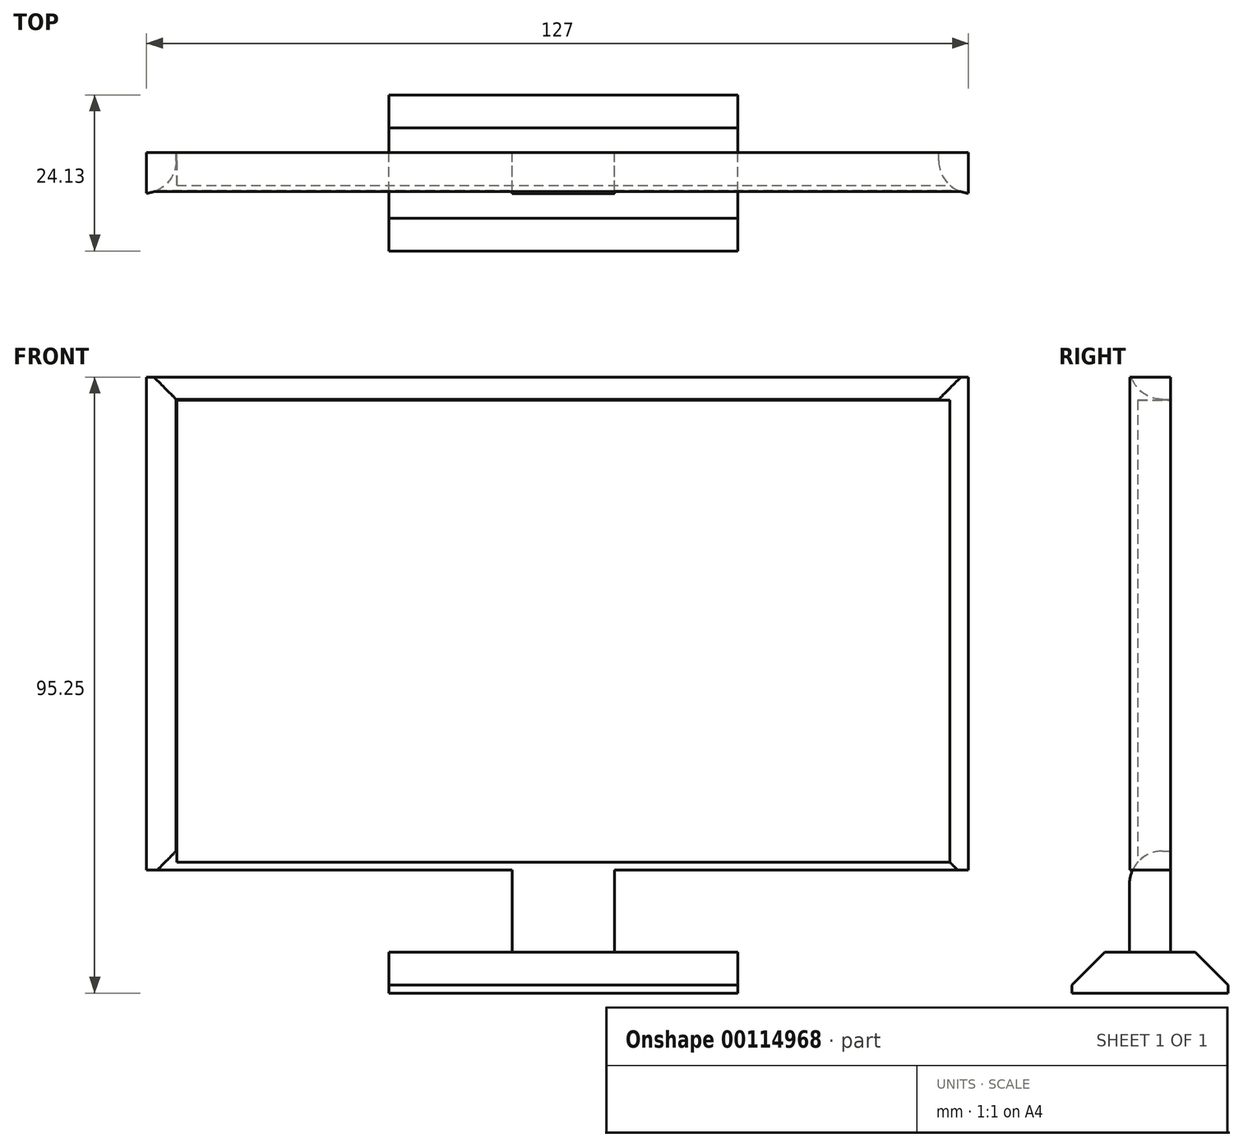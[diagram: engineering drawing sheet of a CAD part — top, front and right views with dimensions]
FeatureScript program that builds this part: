
annotation { "Feature Type Name" : "Feature", "Feature Type Description" : "" }
export const myFeature = defineFeature(function(context is Context, id is Id, definition is map)
    precondition{}
    {
        {
            var Q0;
            Q0=qCreatedBy(makeId("Front.planeOp"),FACE);
            var sketch = newSketch(context, id + "F0", { "sketchPlane" : qUnion([Q0])});
            skLineSegment(sketch, "E0", {"start": v(-63.78, 41.47) * mm, "end": v(63.22, 41.47) * mm});
            skLineSegment(sketch, "E1", {"start": v(-63.78, 41.47) * mm, "end": v(-63.78, -34.73) * mm});
            skLineSegment(sketch, "E2", {"start": v(63.22, 41.47) * mm, "end": v(63.22, -34.73) * mm});
            skLineSegment(sketch, "E3", {"start": v(63.22, -34.73) * mm, "end": v(-63.78, -34.73) * mm});
            skLineSegment(sketch, "E4", {"start": v(8.52, -34.73) * mm, "end": v(8.52, -47.43) * mm});
            skLineSegment(sketch, "E5", {"start": v(-59.2, 38.02) * mm, "end": v(-59.2, -31.83) * mm});
            skLineSegment(sketch, "E6", {"start": v(-59.2, 38.02) * mm, "end": v(58.63, 38.02) * mm});
            skLineSegment(sketch, "E7", {"start": v(58.63, 38.02) * mm, "end": v(58.63, -31.83) * mm});
            skLineSegment(sketch, "E8", {"start": v(-59.2, -31.83) * mm, "end": v(58.63, -31.83) * mm});
            skLineSegment(sketch, "E9", {"start": v(8.52, -47.43) * mm, "end": v(27.57, -47.43) * mm});
            skLineSegment(sketch, "E10", {"start": v(27.57, -47.43) * mm, "end": v(27.57, -53.78) * mm});
            skLineSegment(sketch, "E11", {"start": v(63.22, 15.64) * mm, "end": v(58.63, 15.64) * mm, "construction": true});
            skLineSegment(sketch, "E12", {"start": v(-63.78, 3.1) * mm, "end": v(-59.2, 3.37) * mm, "construction": true});
            skPoint(sketch, "E12.startSnap0", {"position": v(-59.2, 3.1) * mm});
            skPoint(sketch, "E12.endSnap0", {"position": v(-63.78, 3.37) * mm});
            skPoint(sketch, "E12.endSnap1", {"position": v(-59.2, 3.1) * mm});
            skLineSegment(sketch, "E13", {"start": v(-7.28, -34.73) * mm, "end": v(-7.28, -47.43) * mm});
            skLineSegment(sketch, "E14", {"start": v(-7.28, -47.43) * mm, "end": v(-26.33, -47.43) * mm});
            skLineSegment(sketch, "E15", {"start": v(27.57, -53.78) * mm, "end": v(-26.33, -53.78) * mm});
            skLineSegment(sketch, "E16", {"start": v(-26.33, -53.78) * mm, "end": v(-26.33, -47.43) * mm});
            skLineSegment(sketch, "E17", {"start": v(-7.28, -34.73) * mm, "end": v(8.52, -34.73) * mm});
            skLineSegment(sketch, "E18", {"start": v(8.52, -34.73) * mm, "end": v(-7.28, -34.73) * mm});
            skLineSegment(sketch, "E19", {"start": v(8.52, -47.43) * mm, "end": v(-7.28, -47.43) * mm});
            skSolve(sketch);
        }
        {
            var Q0;
            Q0 = qSketchRegion(id + "F0", true);
            extrude(context, id + "F1", {"entities" : qUnion([Q0]), "depth" : 6.35 * mm});
        }
        {
            var Q0;
            Q0=qCreatedBy(makeId("Front.planeOp"),FACE);
            var sketch = newSketch(context, id + "F2", { "sketchPlane" : qUnion([Q0])});
            skLineSegment(sketch, "E20.bottom", {"start": v(-59.13, 37.88) * mm, "end": v(59.35, 37.88) * mm});
            skLineSegment(sketch, "E20.top", {"start": v(-59.13, -31.88) * mm, "end": v(59.35, -31.88) * mm});
            skLineSegment(sketch, "E20.left", {"start": v(-59.13, 37.88) * mm, "end": v(-59.13, -31.88) * mm});
            skLineSegment(sketch, "E20.right", {"start": v(59.35, 37.88) * mm, "end": v(59.35, -31.88) * mm});
            skSolve(sketch);
        }
        {
            var Q0;
            Q0=makeQuery(id+"F2.imprint","IMPRINT",FACE,{"disambiguationData":[TD([[makeQuery(id+"F2.imprint","IMPRINT",EDGE,{"derivedFrom":sQuery(id+"F2.wireOp",EDGE,"E20.bottom")}),-1.0]])]});
            extrude(context, id + "F3", {"entities" : qUnion([Q0]), "operationType" : NewBodyOperationType.ADD, "depth" : 5.08 * mm});
        }
        {
            var Q0;
            Q0=makeQuery(id+"F1.opExtrude","CAP_EDGE",EDGE,{"disambiguationData":[OSD([sQuery(id+"F0.wireOp",EDGE,"E8")])],"isStart":false});
            var Q1;
            Q1=makeQuery(id+"F1.opExtrude","CAP_EDGE",EDGE,{"disambiguationData":[OSD([sQuery(id+"F0.wireOp",EDGE,"E6")])],"isStart":false});
            var Q2;
            Q2=makeQuery(id+"F1.opExtrude","CAP_EDGE",EDGE,{"disambiguationData":[OSD([sQuery(id+"F0.wireOp",EDGE,"E5")])],"isStart":false});
            var Q3;
            Q3=makeQuery(id+"F1.opExtrude","CAP_EDGE",EDGE,{"disambiguationData":[OSD([sQuery(id+"F0.wireOp",EDGE,"E7")])],"isStart":false});
            fillet(context, id + "F4", {"entities" : qUnion([Q0, Q1, Q2, Q3]), "radius" : 5.08 * mm, "tangentPropagation" : true, "allowEdgeOverflow" : false});
        }
        {
            var Q0;
            Q0=makeQuery(id+"F1.opExtrude","CAP_FACE",FACE,{"disambiguationData":[OSD([sQuery(id+"F0.wireOp",EDGE,"E0"),sQuery(id+"F0.wireOp",EDGE,"E1"),sQuery(id+"F0.wireOp",EDGE,"E2"),sQuery(id+"F0.wireOp",EDGE,"E3"),sQuery(id+"F0.wireOp",EDGE,"E4"),sQuery(id+"F0.wireOp",EDGE,"E5"),sQuery(id+"F0.wireOp",EDGE,"E6"),sQuery(id+"F0.wireOp",EDGE,"E7"),sQuery(id+"F0.wireOp",EDGE,"E8"),sQuery(id+"F0.wireOp",EDGE,"E9"),sQuery(id+"F0.wireOp",EDGE,"E10"),sQuery(id+"F0.wireOp",EDGE,"E13"),sQuery(id+"F0.wireOp",EDGE,"E14"),sQuery(id+"F0.wireOp",EDGE,"E15"),sQuery(id+"F0.wireOp",EDGE,"E16")])],"isStart":false});
            var sketch = newSketch(context, id + "F5", { "sketchPlane" : qUnion([Q0])});
            skLineSegment(sketch, "E21", {"start": v(-7.28, -47.43) * mm, "end": v(8.52, -47.43) * mm});
            skLineSegment(sketch, "E22", {"start": v(8.52, -47.43) * mm, "end": v(27.57, -47.43) * mm});
            skLineSegment(sketch, "E23", {"start": v(27.57, -47.43) * mm, "end": v(27.57, -53.78) * mm});
            skLineSegment(sketch, "E24", {"start": v(27.57, -53.78) * mm, "end": v(-26.33, -53.78) * mm});
            skLineSegment(sketch, "E25", {"start": v(-26.33, -53.78) * mm, "end": v(-26.33, -47.43) * mm});
            skLineSegment(sketch, "E26", {"start": v(-26.33, -47.43) * mm, "end": v(-7.28, -47.43) * mm});
            skSolve(sketch);
        }
        {
            var Q0;
            Q0=makeQuery(id+"F3.boolean.opBoolean","MERGE",FACE,{"derivedFrom":[makeQuery(id+"F1.opExtrude","CAP_FACE",FACE,{"disambiguationData":[OSD([sQuery(id+"F0.wireOp",EDGE,"E0"),sQuery(id+"F0.wireOp",EDGE,"E1"),sQuery(id+"F0.wireOp",EDGE,"E2"),sQuery(id+"F0.wireOp",EDGE,"E3"),sQuery(id+"F0.wireOp",EDGE,"E4"),sQuery(id+"F0.wireOp",EDGE,"E5"),sQuery(id+"F0.wireOp",EDGE,"E6"),sQuery(id+"F0.wireOp",EDGE,"E7"),sQuery(id+"F0.wireOp",EDGE,"E8"),sQuery(id+"F0.wireOp",EDGE,"E9"),sQuery(id+"F0.wireOp",EDGE,"E10"),sQuery(id+"F0.wireOp",EDGE,"E13"),sQuery(id+"F0.wireOp",EDGE,"E14"),sQuery(id+"F0.wireOp",EDGE,"E15"),sQuery(id+"F0.wireOp",EDGE,"E16")])],"isStart":true}),makeQuery(id+"F3.opExtrude","CAP_FACE",FACE,{"disambiguationData":[OSD([sQuery(id+"F2.wireOp",EDGE,"E20.bottom"),sQuery(id+"F2.wireOp",EDGE,"E20.top"),sQuery(id+"F2.wireOp",EDGE,"E20.left"),sQuery(id+"F2.wireOp",EDGE,"E20.right")])],"isStart":true})]});
            var sketch = newSketch(context, id + "F6", { "sketchPlane" : qUnion([Q0])});
            skLineSegment(sketch, "E27", {"start": v(-27.57, -47.43) * mm, "end": v(26.33, -47.43) * mm});
            skLineSegment(sketch, "E28", {"start": v(26.33, -47.43) * mm, "end": v(26.33, -53.78) * mm});
            skLineSegment(sketch, "E29", {"start": v(26.33, -53.78) * mm, "end": v(-27.57, -53.78) * mm});
            skLineSegment(sketch, "E30", {"start": v(-27.57, -53.78) * mm, "end": v(-27.57, -47.43) * mm});
            skSolve(sketch);
        }
        {
            var Q0;
            {var subQ0=sQuery(id+"F6.wireOp",EDGE,"E28");Q0=makeQuery(id+"F6.imprint","IMPRINT",FACE,{"disambiguationData":[TD([[makeQuery(id+"F6.imprint","IMPRINT",EDGE,{"derivedFrom":subQ0}),1.0]])]});}
            extrude(context, id + "F7", {"entities" : qUnion([Q0]), "operationType" : NewBodyOperationType.ADD, "depth" : 8.9 * mm});
        }
        {
            var Q0;
            Q0=makeQuery(id+"F5.imprint","IMPRINT",FACE,{"disambiguationData":[TD([[makeQuery(id+"F5.imprint","IMPRINT",EDGE,{"derivedFrom":sQuery(id+"F5.wireOp",EDGE,"E21")}),-1.0]])]});
            extrude(context, id + "F8", {"entities" : qUnion([Q0]), "operationType" : NewBodyOperationType.ADD, "depth" : 8.9 * mm});
        }
        {
            var Q0;
            Q0=makeQuery(id+"F7.opExtrude","CAP_EDGE",EDGE,{"disambiguationData":[OSD([sQuery(id+"F6.wireOp",EDGE,"E27")])],"isStart":false});
            var Q1;
            Q1=makeQuery(id+"F8.opExtrude","CAP_EDGE",EDGE,{"disambiguationData":[OSD([sQuery(id+"F5.wireOp",EDGE,"E21"),sQuery(id+"F5.wireOp",EDGE,"E22"),sQuery(id+"F5.wireOp",EDGE,"E26")])],"isStart":false});
            chamfer(context, id + "F9", {"entities" : qUnion([Q0, Q1]), "width" : 5.08 * mm, "tangentPropagation" : true});
        }
    });
